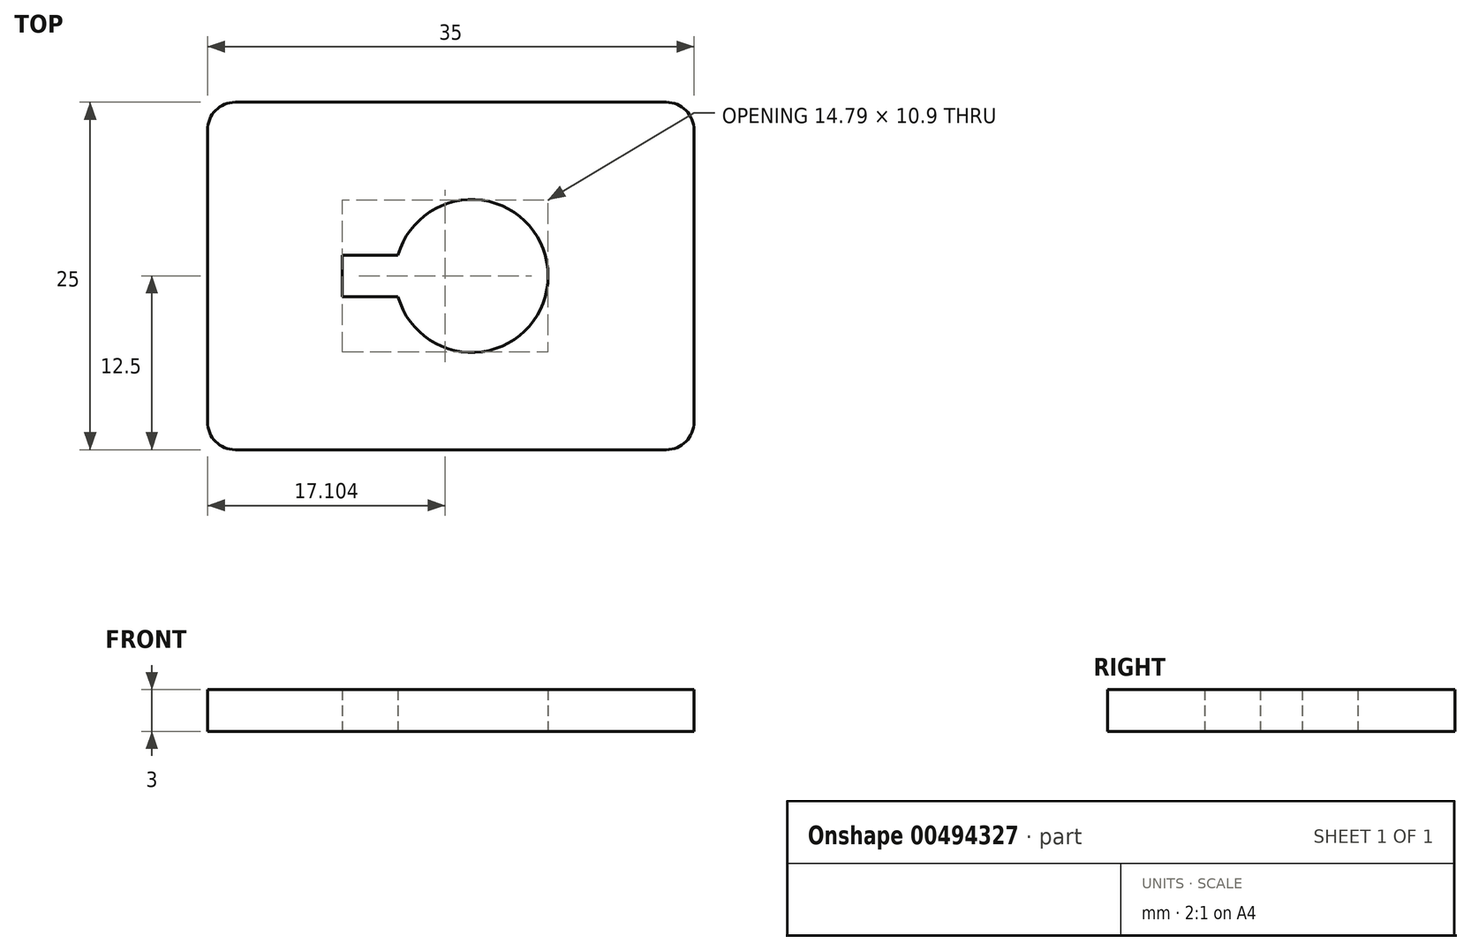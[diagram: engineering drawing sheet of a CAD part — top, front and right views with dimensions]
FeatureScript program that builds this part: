
annotation { "Feature Type Name" : "Feature", "Feature Type Description" : "" }
export const myFeature = defineFeature(function(context is Context, id is Id, definition is map)
    precondition{}
    {
        {
            var Q0;
            Q0=qCreatedBy(makeId("Top.planeOp"),FACE);
            var sketch = newSketch(context, id + "F0", { "sketchPlane" : qUnion([Q0])});
            skLineSegment(sketch, "E0.bottom", {"start": v(16, 12.5) * mm, "end": v(-19, 12.5) * mm});
            skLineSegment(sketch, "E0.top", {"start": v(16, -12.5) * mm, "end": v(-19, -12.5) * mm});
            skLineSegment(sketch, "E0.left", {"start": v(16, 12.5) * mm, "end": v(16, -12.5) * mm});
            skLineSegment(sketch, "E0.right", {"start": v(-19, 12.5) * mm, "end": v(-19, -12.5) * mm});
            skPoint(sketch, "E0.middle", {"position": v(0, 0) * mm});
            skCircle(sketch, "E1", {"center": v(0, 0) * mm, "radius": 5.5 * mm});
            skLineSegment(sketch, "E2.bottom", {"start": v(-9.3, 1.5) * mm, "end": v(-5.3, 1.5) * mm});
            skLineSegment(sketch, "E2.top", {"start": v(-9.3, -1.5) * mm, "end": v(-5.3, -1.5) * mm});
            skLineSegment(sketch, "E2.left", {"start": v(-9.3, 1.5) * mm, "end": v(-9.3, -1.5) * mm});
            skPoint(sketch, "E2.middle", {"position": v(-5.5, 0) * mm});
            skPoint(sketch, "E3", {"position": v(-5.3, 1.5) * mm});
            skPoint(sketch, "E4", {"position": v(-5.3, -1.5) * mm});
            skSolve(sketch);
        }
        {
            var Q0;
            Q0=makeQuery(id+"F0.imprint","IMPRINT",FACE,{"disambiguationData":[TD([[makeQuery(id+"F0.imprint","IMPRINT",EDGE,{"derivedFrom":sQuery(id+"F0.wireOp",EDGE,"E0.bottom")}),1.0]])]});
            extrude(context, id + "F1", {"entities" : qUnion([Q0]), "depth" : 3 * mm});
        }
        {
            var Q0;
            Q0=makeQuery(id+"F1.opExtrude","SWEPT_EDGE",EDGE,{"disambiguationData":[OSD([sQuery(id+"F0.wireOp",EDGE,"E0.top"),sQuery(id+"F0.wireOp",EDGE,"E0.right")])]});
            var Q1;
            Q1=makeQuery(id+"F1.opExtrude","SWEPT_EDGE",EDGE,{"disambiguationData":[OSD([sQuery(id+"F0.wireOp",EDGE,"E0.top"),sQuery(id+"F0.wireOp",EDGE,"E0.left")])]});
            var Q2;
            Q2=makeQuery(id+"F1.opExtrude","SWEPT_EDGE",EDGE,{"disambiguationData":[OSD([sQuery(id+"F0.wireOp",EDGE,"E0.bottom"),sQuery(id+"F0.wireOp",EDGE,"E0.left")])]});
            var Q3;
            Q3=makeQuery(id+"F1.opExtrude","SWEPT_EDGE",EDGE,{"disambiguationData":[OSD([sQuery(id+"F0.wireOp",EDGE,"E0.bottom"),sQuery(id+"F0.wireOp",EDGE,"E0.right")])]});
            fillet(context, id + "F2", {"entities" : qUnion([Q0, Q1, Q2, Q3]), "radius" : 2 * mm, "tangentPropagation" : true, "allowEdgeOverflow" : false});
        }
    });
